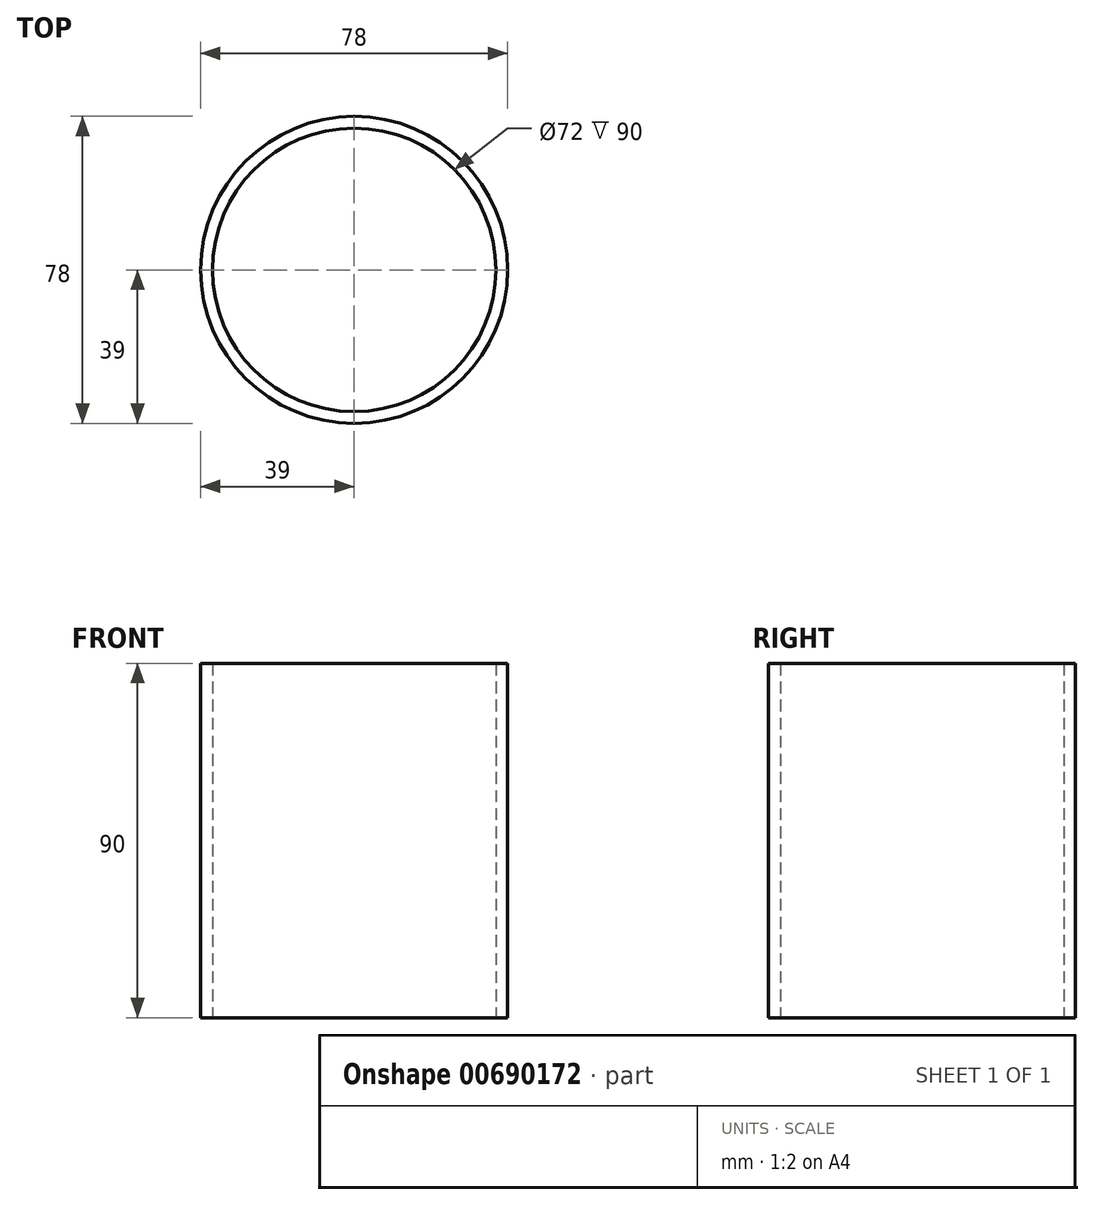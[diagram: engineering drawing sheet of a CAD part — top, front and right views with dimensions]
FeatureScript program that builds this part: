
annotation { "Feature Type Name" : "Feature", "Feature Type Description" : "" }
export const myFeature = defineFeature(function(context is Context, id is Id, definition is map)
    precondition{}
    {
        {
            var Q0;
            Q0=qCreatedBy(makeId("Top.planeOp"),FACE);
            var sketch = newSketch(context, id + "F0", { "sketchPlane" : qUnion([Q0])});
            skCircle(sketch, "E0", {"center": v(0, 0) * mm, "radius": 39 * mm});
            skCircle(sketch, "E1", {"center": v(0, 0) * mm, "radius": 36 * mm});
            skSolve(sketch);
        }
        {
            var Q0;
            Q0 = qSketchRegion(id + "F0", true);
            extrude(context, id + "F1", {"entities" : qUnion([Q0]), "depth" : 90 * mm, "offsetDistance" : 25 * mm});
        }
    });
